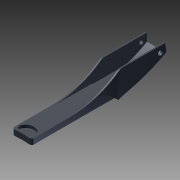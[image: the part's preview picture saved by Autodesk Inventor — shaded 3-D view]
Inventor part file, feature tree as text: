
AUTODESK INVENTOR PART (.ipt)
format: ipt  version: 2011 (Build 150239000, 239)  size: 525,824 bytes
history: native  units: mm (DEFAULTED — no unit token found)
features: other x5, extrude x4, plane x4, sketch x4, fillet x1, imported_body x1
ambient origin geometry x8: Origin, YZ Plane, XZ Plane, XY Plane, X Axis, Y Axis, Z Axis, Center Point
bodies: Solid1 (feature_tree)
feature tree (19):
  other  "Bottom - Master.ipt"
  extrude  "Extrusion1"  Depth=38.1mm
  plane  "Work Plane1"
  plane  "Work Plane2"
  plane  "Work Plane3"
  plane  "Work Plane4"
  other  "Side Cut"
  extrude  "Extrusion2"  Depth=114.3mm
  extrude  "Extrusion5"  Depth=12.7mm
  extrude  "Extrusion6"  Depth=19.05mm
  fillet  "Fillet2"  Radius=15.875mm
  other  "Split Line"
  other  "Hinge"
  sketch  "Sketch3"  dims[d1=10.0mm d4=38.1mm]
  other  "Srf1"
  sketch  "Sketch7"  dims[d6=1.524mm d7=0.0mm d14=114.3mm]
  sketch  "Sketch9"  dims[d16=25.4mm d17=0.0mm d25=12.7mm]
  sketch  "Sketch10"  dims[d26=25.4mm d27=0.0mm d29=19.05mm d30=15.875mm d31=9.525mm d33=3.175mm d34=0.0mm d35=3.175mm d40=96.1136mm d42=-34.925mm d43=34.925mm d45=11.1252mm d46=38.1mm d47=25.4mm d48=0.0mm d49=25.4mm d50=0.0mm]
  imported_body  "DerivedBody::Bottom - Master.ipt"
